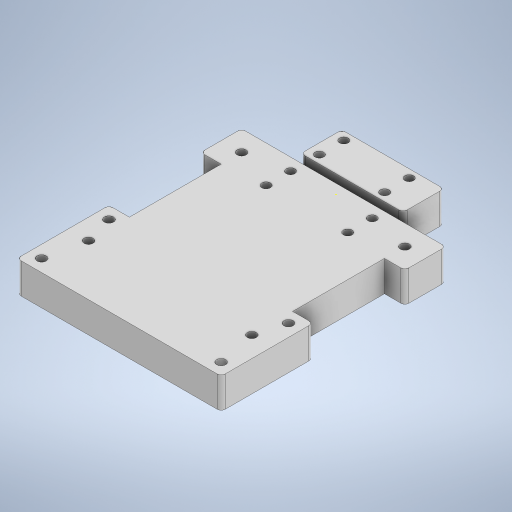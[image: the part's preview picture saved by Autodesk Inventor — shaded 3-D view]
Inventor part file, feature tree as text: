
AUTODESK INVENTOR PART (.ipt)
format: ipt  version: 2024 (Build 280153000, 153)  size: 320,512 bytes
history: native  units: mm
features: sketch x5, extrude x3, fillet x1, projected_geometry x1
ambient origin geometry x8: Origin, YZ Plane, XZ Plane, XY Plane, X Axis, Y Axis, Z Axis, Center Point
bodies: Solid1 (feature_tree)
feature tree (10):
  extrude  "Extrusion1"  Depth=110.0mm
  sketch  "Sketch2"  dims[d2=15.0mm d3=0.0mm d6=20.0mm]
  sketch  "Sketch3"  dims[d7=20.0mm d8=10.0mm d9=10.0mm]
  extrude  "Extrusion2"  Depth=20.0mm
  extrude  "Extrusion4"  Depth=10.0mm
  fillet  "Fillet1"  Radius=10.0mm
  sketch  "Sketch1"  dims[d0=100.0mm d1=110.0mm]
  sketch  "Sketch4"  dims[d10=45.0mm]
  projected_geometry  "Projected Loop1"
  sketch  "Sketch6"  dims[d11=45.0mm d12=15.0mm d13=0.0mm d19=20.0mm d20=20.0mm d21=10.0mm d22=10.0mm d23=18.0mm d24=18.0mm d25=20.0mm d26=20.0mm d27=4.2mm d28=4.2mm d29=6.0mm d30=25.0mm d31=25.0mm d32=4.1mm d33=20.0mm d34=4.0mm d35=4.0mm d36=4.0mm d37=4.0mm d38=12.0mm d39=12.0mm d40=15.0mm d41=0.0mm d42=2.0mm]
